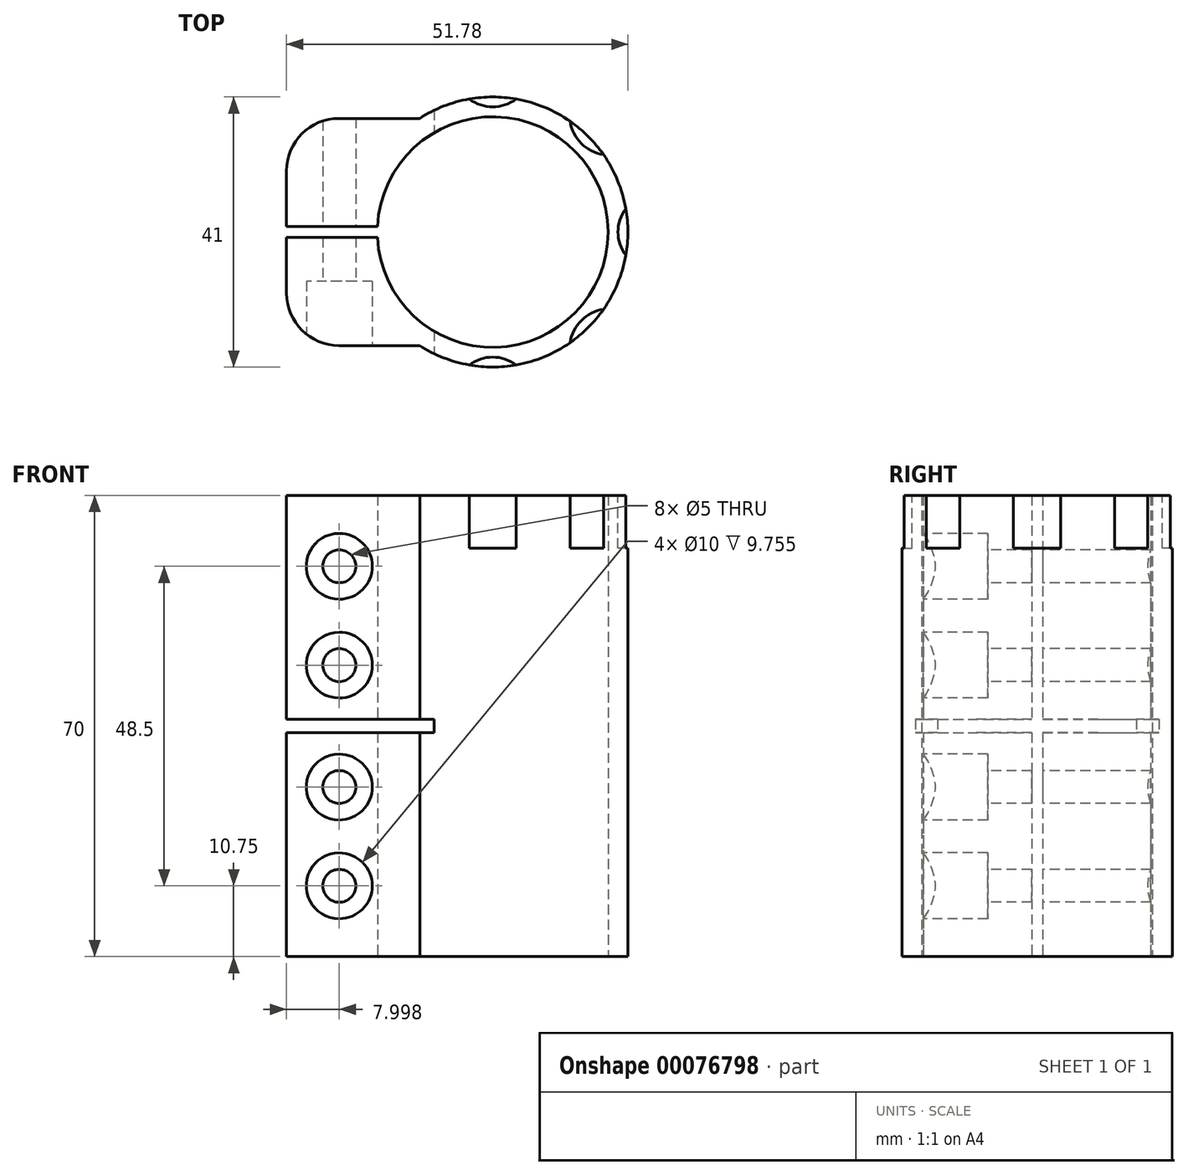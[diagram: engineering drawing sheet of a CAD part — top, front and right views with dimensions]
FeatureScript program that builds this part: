
annotation { "Feature Type Name" : "Feature", "Feature Type Description" : "" }
export const myFeature = defineFeature(function(context is Context, id is Id, definition is map)
    precondition{}
    {
        {
            var Q0;
            Q0=qCreatedBy(makeId("Top.planeOp"),FACE);
            var sketch = newSketch(context, id + "F0", { "sketchPlane" : qUnion([Q0])});
            skArc(sketch, "E0", {"start": v(-17.48, -0.85) * mm, "mid": v(17.5, 0) * mm, "end": v(-17.48, 0.85) * mm});
            skArc(sketch, "E1", {"start": v(-11.08, -17.25) * mm, "mid": v(20.5, 0) * mm, "end": v(-11.08, 17.25) * mm});
            skLineSegment(sketch, "E2", {"start": v(-11.08, 17.25) * mm, "end": v(-23.28, 17.25) * mm});
            skLineSegment(sketch, "E3", {"start": v(-31.28, 9.25) * mm, "end": v(-31.28, 0.85) * mm});
            skLineSegment(sketch, "E4", {"start": v(-31.28, 0.85) * mm, "end": v(-20.48, 0.85) * mm});
            skPoint(sketch, "E5.visualSharp", {"position": v(-31.28, 17.25) * mm});
            skArc(sketch, "E5.filletArc", {"start": v(-23.28, 17.25) * mm, "mid": v(-28.94, 14.9) * mm, "end": v(-31.28, 9.25) * mm});
            skLineSegment(sketch, "E6", {"start": v(0, 0) * mm, "end": v(31.62, 0) * mm, "construction": true});
            skLineSegment(sketch, "E7.MirrorCS", {"start": v(-31.28, -0.85) * mm, "end": v(-20.48, -0.85) * mm});
            skLineSegment(sketch, "E8.MirrorCS", {"start": v(-11.08, -17.25) * mm, "end": v(-23.28, -17.25) * mm});
            skLineSegment(sketch, "E9.MirrorCS", {"start": v(-31.28, -9.25) * mm, "end": v(-31.28, -0.85) * mm});
            skArc(sketch, "E10.MirrorCS", {"start": v(-23.28, -17.25) * mm, "mid": v(-28.94, -14.9) * mm, "end": v(-31.28, -9.25) * mm});
            skLineSegment(sketch, "E11", {"start": v(-20.48, 0.85) * mm, "end": v(-17.48, 0.85) * mm});
            skLineSegment(sketch, "E12", {"start": v(-20.48, -0.85) * mm, "end": v(-17.48, -0.85) * mm});
            skSolve(sketch);
        }
        {
            var Q0;
            Q0 = qSketchRegion(id + "F0", true);
            extrude(context, id + "F1", {"entities" : qUnion([Q0]), "endBound" : BoundingType.SYMMETRIC, "depth" : 70 * mm});
        }
        {
            var Q0;
            Q0=makeQuery(id+"F1.opExtrude","SWEPT_FACE",FACE,{"disambiguationData":[OSD([sQuery(id+"F0.wireOp",EDGE,"E8.MirrorCS")])]});
            var sketch = newSketch(context, id + "F2", { "sketchPlane" : qUnion([Q0])});
            skPoint(sketch, "E13", {"position": v(-5.74, 0) * mm});
            skPoint(sketch, "E14", {"position": v(-23.28, -24.25) * mm});
            skPoint(sketch, "E15", {"position": v(-23.28, -9.25) * mm});
            skPoint(sketch, "E16", {"position": v(-23.28, 9.25) * mm});
            skPoint(sketch, "E17", {"position": v(-23.28, 24.25) * mm});
            skSolve(sketch);
        }
        {
            var Q0;
            Q0=sQuery(id+"F2.wireOp",VERTEX,"E14");
            var Q1;
            Q1=sQuery(id+"F2.wireOp",VERTEX,"E15");
            var Q2;
            Q2=sQuery(id+"F2.wireOp",VERTEX,"E16");
            var Q3;
            Q3=sQuery(id+"F2.wireOp",VERTEX,"E17");
            var Q4;
            Q4=makeQuery(id+"F1.opExtrude","SWEPT_BODY",BODY,{"disambiguationData":[OSD([sQuery(id+"F0.wireOp",EDGE,"E0"),sQuery(id+"F0.wireOp",EDGE,"E1"),sQuery(id+"F0.wireOp",EDGE,"E2"),sQuery(id+"F0.wireOp",EDGE,"E3"),sQuery(id+"F0.wireOp",EDGE,"E4"),sQuery(id+"F0.wireOp",EDGE,"E5.filletArc"),sQuery(id+"F0.wireOp",EDGE,"E7.MirrorCS"),sQuery(id+"F0.wireOp",EDGE,"E8.MirrorCS"),sQuery(id+"F0.wireOp",EDGE,"E9.MirrorCS"),sQuery(id+"F0.wireOp",EDGE,"E10.MirrorCS"),sQuery(id+"F0.wireOp",EDGE,"E11"),sQuery(id+"F0.wireOp",EDGE,"E12")])]});
            hole(context, id + "F3", {"style" : HoleStyle.C_BORE, "endStyle" : HoleEndStyle.THROUGH, "holeDiameter" : 5 * mm, "cBoreDiameter" : 10 * mm, "cBoreDepth" : 8 * mm, "locations" : qUnion([Q0, Q1, Q2, Q3]), "scope" : qUnion([Q4]), "isTappedThrough" : true});
        }
        {
            var Q0;
            Q0=makeQuery(id+"F1.opExtrude","SWEPT_FACE",FACE,{"disambiguationData":[OSD([sQuery(id+"F0.wireOp",EDGE,"E8.MirrorCS")])]});
            var sketch = newSketch(context, id + "F4", { "sketchPlane" : qUnion([Q0])});
            skLineSegment(sketch, "E18.bottom", {"start": v(-31.28, 1) * mm, "end": v(-8.88, 1) * mm});
            skLineSegment(sketch, "E18.top", {"start": v(-31.28, -1) * mm, "end": v(-8.88, -1) * mm});
            skLineSegment(sketch, "E18.left", {"start": v(-31.28, 1) * mm, "end": v(-31.28, -1) * mm});
            skLineSegment(sketch, "E18.right", {"start": v(-8.88, 1) * mm, "end": v(-8.88, -1) * mm});
            skSolve(sketch);
        }
        {
            var Q0;
            Q0 = qSketchRegion(id + "F4", true);
            extrude(context, id + "F5", {"entities" : qUnion([Q0]), "operationType" : NewBodyOperationType.REMOVE, "endBound" : BoundingType.SYMMETRIC, "oppositeDirection" : true, "depth" : 700 * mm});
        }
        {
            var Q0;
            Q0=makeQuery(id+"F1.opExtrude","CAP_FACE",FACE,{"disambiguationData":[OSD([sQuery(id+"F0.wireOp",EDGE,"E0"),sQuery(id+"F0.wireOp",EDGE,"E1"),sQuery(id+"F0.wireOp",EDGE,"E2"),sQuery(id+"F0.wireOp",EDGE,"E3"),sQuery(id+"F0.wireOp",EDGE,"E4"),sQuery(id+"F0.wireOp",EDGE,"E5.filletArc"),sQuery(id+"F0.wireOp",EDGE,"E7.MirrorCS"),sQuery(id+"F0.wireOp",EDGE,"E8.MirrorCS"),sQuery(id+"F0.wireOp",EDGE,"E9.MirrorCS"),sQuery(id+"F0.wireOp",EDGE,"E10.MirrorCS"),sQuery(id+"F0.wireOp",EDGE,"E11"),sQuery(id+"F0.wireOp",EDGE,"E12")])],"isStart":false});
            var sketch = newSketch(context, id + "F6", { "sketchPlane" : qUnion([Q0])});
            skCircle(sketch, "E19", {"center": v(0, -25) * mm, "radius": 6 * mm});
            skCircle(sketch, "E20.1.0", {"center": v(17.68, -17.68) * mm, "radius": 6 * mm});
            skCircle(sketch, "E20.2.0", {"center": v(25, 0) * mm, "radius": 6 * mm});
            skCircle(sketch, "E20.3.0", {"center": v(17.68, 17.68) * mm, "radius": 6 * mm});
            skCircle(sketch, "E20.4.0", {"center": v(0, 25) * mm, "radius": 6 * mm});
            skPoint(sketch, "E20.center", {"position": v(0, 0) * mm});
            skLineSegment(sketch, "E20.anchor1", {"start": v(0, 0) * mm, "end": v(0, -25) * mm, "construction": true});
            skLineSegment(sketch, "E20.anchor2", {"start": v(0, 0) * mm, "end": v(0, 25) * mm, "construction": true});
            skSolve(sketch);
        }
        {
            var Q0;
            {var subQ0=sQuery(id+"F6.wireOp",EDGE,"E19");var subQ1=makeQuery(id+"F1.opExtrude","CAP_EDGE",EDGE,{"disambiguationData":[OSD([sQuery(id+"F0.wireOp",EDGE,"E1")])],"isStart":false});var subQ2=makeQuery(id+"F6.imprint","INTERSECT",VERTEX,{"disambiguationData":[OD(0.0)],"derivedFrom":[subQ1,subQ0]});Q0=makeQuery(id+"F6.imprint","IMPRINT",FACE,{"disambiguationData":[TD([[makeQuery(id+"F6.imprint","IMPRINT",EDGE,{"disambiguationData":[TD([[subQ2,1.0]])],"derivedFrom":subQ0}),1.0]])]});}
            var Q1;
            {var subQ0=sQuery(id+"F6.wireOp",EDGE,"E20.1.0");var subQ1=makeQuery(id+"F1.opExtrude","CAP_EDGE",EDGE,{"disambiguationData":[OSD([sQuery(id+"F0.wireOp",EDGE,"E1")])],"isStart":false});var subQ2=makeQuery(id+"F6.imprint","INTERSECT",VERTEX,{"disambiguationData":[OD(0.0)],"derivedFrom":[subQ1,subQ0]});Q1=makeQuery(id+"F6.imprint","IMPRINT",FACE,{"disambiguationData":[TD([[makeQuery(id+"F6.imprint","IMPRINT",EDGE,{"disambiguationData":[TD([[subQ2,1.0]])],"derivedFrom":subQ0}),1.0]])]});}
            var Q2;
            {var subQ0=sQuery(id+"F6.wireOp",EDGE,"E20.2.0");var subQ1=makeQuery(id+"F1.opExtrude","CAP_EDGE",EDGE,{"disambiguationData":[OSD([sQuery(id+"F0.wireOp",EDGE,"E1")])],"isStart":false});var subQ2=makeQuery(id+"F6.imprint","INTERSECT",VERTEX,{"disambiguationData":[OD(0.0)],"derivedFrom":[subQ1,subQ0]});Q2=makeQuery(id+"F6.imprint","IMPRINT",FACE,{"disambiguationData":[TD([[makeQuery(id+"F6.imprint","IMPRINT",EDGE,{"disambiguationData":[TD([[subQ2,1.0]])],"derivedFrom":subQ0}),1.0]])]});}
            var Q3;
            {var subQ0=sQuery(id+"F6.wireOp",EDGE,"E20.3.0");var subQ1=makeQuery(id+"F1.opExtrude","CAP_EDGE",EDGE,{"disambiguationData":[OSD([sQuery(id+"F0.wireOp",EDGE,"E1")])],"isStart":false});var subQ2=makeQuery(id+"F6.imprint","INTERSECT",VERTEX,{"disambiguationData":[OD(0.0)],"derivedFrom":[subQ1,subQ0]});Q3=makeQuery(id+"F6.imprint","IMPRINT",FACE,{"disambiguationData":[TD([[makeQuery(id+"F6.imprint","IMPRINT",EDGE,{"disambiguationData":[TD([[subQ2,-1.0]])],"derivedFrom":subQ0}),1.0]])]});}
            var Q4;
            {var subQ0=sQuery(id+"F6.wireOp",EDGE,"E20.4.0");var subQ1=makeQuery(id+"F1.opExtrude","CAP_EDGE",EDGE,{"disambiguationData":[OSD([sQuery(id+"F0.wireOp",EDGE,"E1")])],"isStart":false});var subQ2=makeQuery(id+"F6.imprint","INTERSECT",VERTEX,{"disambiguationData":[OD(0.0)],"derivedFrom":[subQ1,subQ0]});Q4=makeQuery(id+"F6.imprint","IMPRINT",FACE,{"disambiguationData":[TD([[makeQuery(id+"F6.imprint","IMPRINT",EDGE,{"disambiguationData":[TD([[subQ2,-1.0]])],"derivedFrom":subQ0}),1.0]])]});}
            extrude(context, id + "F7", {"entities" : qUnion([Q0, Q1, Q2, Q3, Q4]), "operationType" : NewBodyOperationType.REMOVE, "oppositeDirection" : true, "depth" : 8 * mm});
        }
    });
